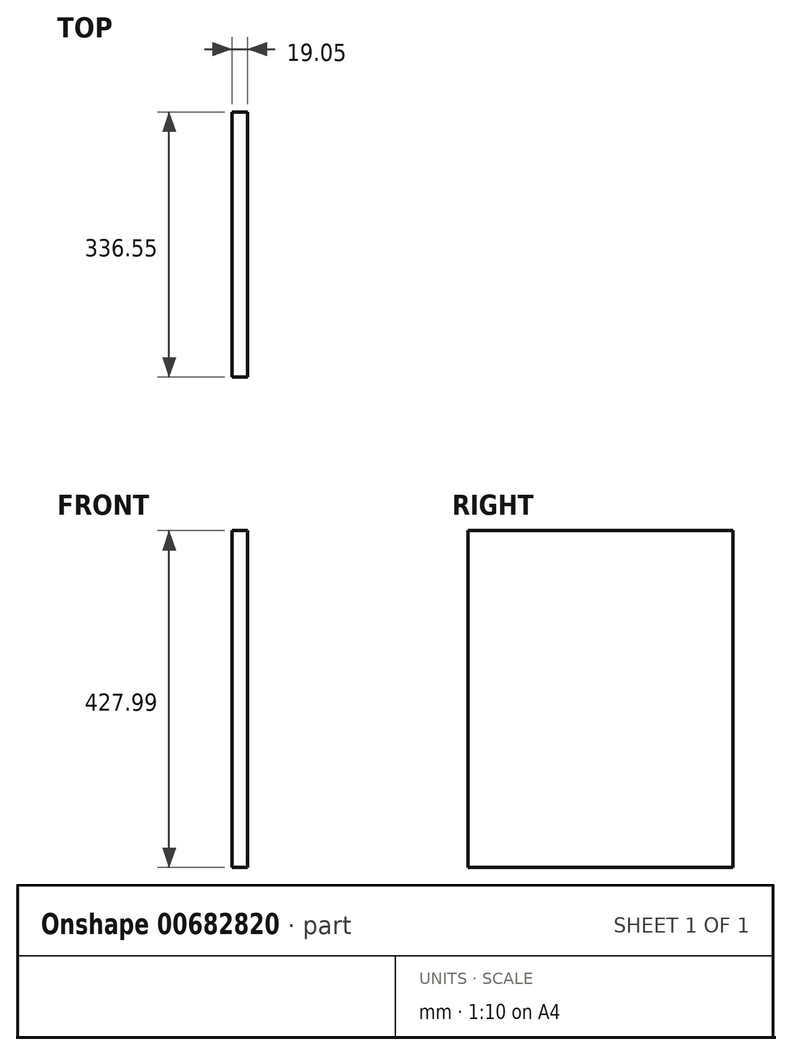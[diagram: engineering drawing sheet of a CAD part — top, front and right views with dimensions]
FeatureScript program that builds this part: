
annotation { "Feature Type Name" : "Feature", "Feature Type Description" : "" }
export const myFeature = defineFeature(function(context is Context, id is Id, definition is map)
    precondition{}
    {
        {
            var Q0;
            Q0=qCreatedBy(makeId("Right.planeOp"),FACE);
            var sketch = newSketch(context, id + "F0", { "sketchPlane" : qUnion([Q0])});
            skLineSegment(sketch, "E0.bottom", {"start": v(0, 0) * mm, "end": v(-336.55, 0) * mm});
            skLineSegment(sketch, "E0.top", {"start": v(0, 428) * mm, "end": v(-336.55, 428) * mm});
            skLineSegment(sketch, "E0.left", {"start": v(0, 0) * mm, "end": v(0, 428) * mm});
            skLineSegment(sketch, "E0.right", {"start": v(-336.55, 0) * mm, "end": v(-336.55, 428) * mm});
            skSolve(sketch);
        }
        {
            var Q0;
            Q0 = qSketchRegion(id + "F0", true);
            extrude(context, id + "F1", {"entities" : qUnion([Q0]), "depth" : 19.05 * mm, "offsetDistance" : 25.4 * mm});
        }
    });
